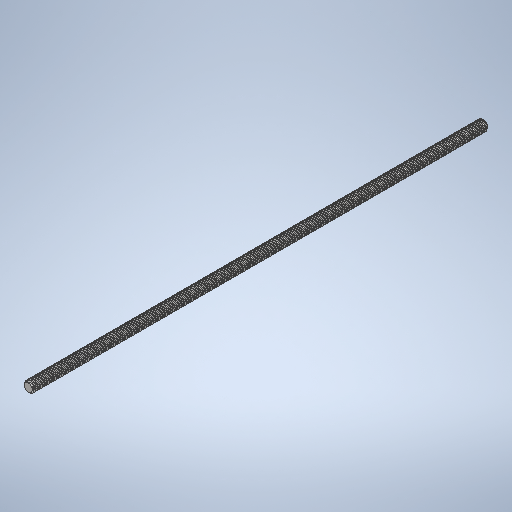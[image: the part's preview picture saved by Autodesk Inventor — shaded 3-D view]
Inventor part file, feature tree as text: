
AUTODESK INVENTOR PART (.ipt)
format: ipt  version: 2025.2 (Build 292293000, 293)  size: 1,367,040 bytes
history: native  units: mm
features: extrude x1, chamfer x1, other x1, pattern_circular x1
ambient origin geometry x8: Origin, YZ Plane, XZ Plane, XY Plane, X Axis, Y Axis, Z Axis, Center Point
bodies: Solid1 (feature_tree)
feature tree (4):
  extrude  "1000mm Rod"  Depth=350.0mm TaperAngle=0.0deg
  chamfer  "Chamfer1"  Distance=0.907143mm Angle=45.0deg
  other  "ACME Thread 2mm Pitch"
  pattern_circular  "4 Start"  [2 undecoded]
note: 2 required parameter values undecoded (feature->parameter linkage not recoverable at this tier; creation-order binding heuristic only, values carry confidence <= 0.55)
